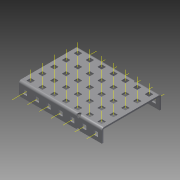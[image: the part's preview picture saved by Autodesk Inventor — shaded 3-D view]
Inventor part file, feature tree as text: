
AUTODESK INVENTOR PART (.ipt)
format: ipt  version: 2015 (Build 190159000, 159)  size: 2,476,544 bytes
history: native  units: in
note: dims shown in document units (in); Inventor stores cm internally (conversion verified against a paired STEP export)
features: other x55, pattern_linear x2, sheet_metal_op x1, extrude x1, imported_body x1, sketch x1
ambient origin geometry x8: Origin, YZ Plane, XZ Plane, XY Plane, X Axis, Y Axis, Z Axis, Center Point
bodies: Body1 (feature_tree)
feature tree (61):
  sheet_metal_op  "Fold1"
  other  "C-Channel"
  extrude  "length cut"  Depth=0.5in
  other  "top axis"
  other  "front axis"
  other  "back axis"
  pattern_linear  "top axes"  Spacing1=0.5in  [1 undecoded]
  pattern_linear  "horiz axes"  Spacing1=0.0in  [1 undecoded]
  other  "right plane"
  imported_body  "Base1"
  sketch  "Sketch1"  dims[d1=0.0in d4=0.5in d5=1.9685in d7=0.5in d10=0.5in d11=0.0in d12=0.0in d13=0.0in d14=-3.5in d15=0.0in d16=0.0in]
  other  "Work Point1"
  other  "Work Axis6"
  other  "Work Axis11"
  other  "Work Axis16"
  other  "Work Axis21"
  other  "Work Point2"
  other  "Work Point3"
  other  "Work Axis36"
  other  "Work Axis37"
  other  "Work Axis38"
  other  "Work Axis39"
  other  "Work Axis40"
  other  "Work Axis60"
  other  "Work Axis61"
  other  "Work Axis62"
  other  "Work Axis63"
  other  "Work Axis64"
  other  "Work Axis84"
  other  "Work Axis85"
  other  "Work Axis86"
  other  "Work Axis87"
  other  "Work Axis88"
  other  "Work Axis108"
  other  "Work Axis109"
  other  "Work Axis110"
  other  "Work Axis111"
  other  "Work Axis112"
  other  "Work Axis132"
  other  "Work Axis133"
  other  "Work Axis134"
  other  "Work Axis135"
  other  "Work Axis136"
  other  "Work Axis156"
  other  "Work Axis157"
  other  "Work Axis158"
  other  "Work Axis159"
  other  "Work Axis160"
  other  "Work Axis180"
  other  "Work Axis181"
  other  "Work Axis182"
  other  "Work Axis183"
  other  "Work Axis184"
  other  "left plane"
  other  "Work Axis400"
  other  "Work Axis401"
  other  "Work Axis402"
  other  "Work Axis403"
  other  "Work Axis404"
  other  "Work Axis405"
  other  "Work Axis406"
note: 2 required parameter values undecoded (feature->parameter linkage not recoverable at this tier; creation-order binding heuristic only, values carry confidence <= 0.55)
